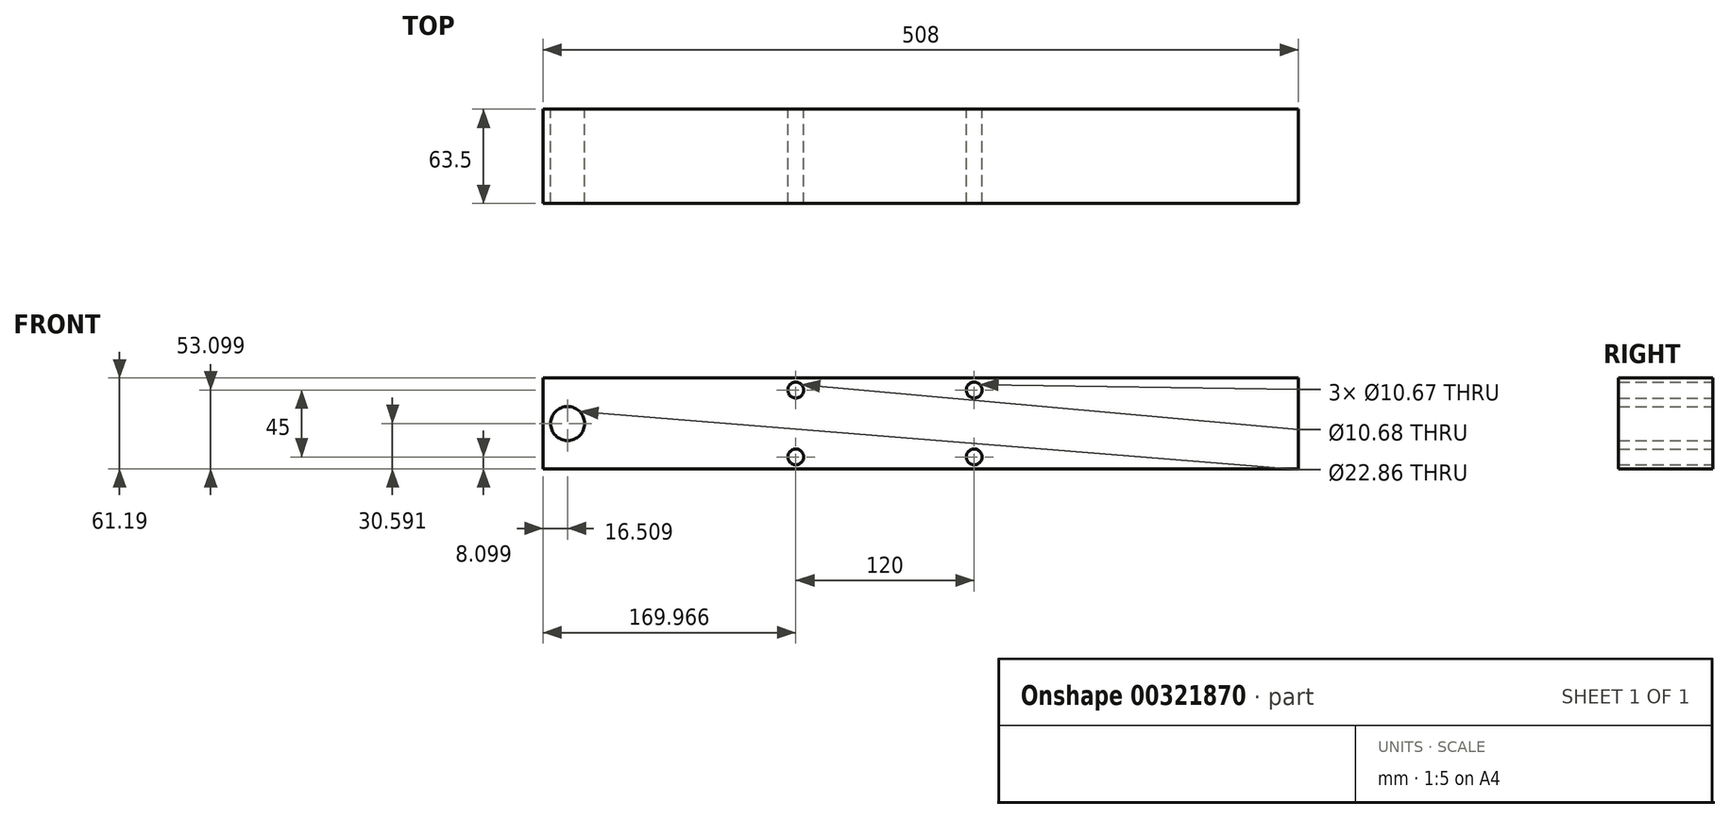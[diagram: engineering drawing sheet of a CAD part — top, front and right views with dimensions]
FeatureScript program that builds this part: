
annotation { "Feature Type Name" : "Feature", "Feature Type Description" : "" }
export const myFeature = defineFeature(function(context is Context, id is Id, definition is map)
    precondition{}
    {
        {
            var Q0;
            Q0=qCreatedBy(makeId("Front.planeOp"),FACE);
            var sketch = newSketch(context, id + "F0", { "sketchPlane" : qUnion([Q0])});
            skLineSegment(sketch, "E0.bottom", {"start": v(-114.58, 33.33) * mm, "end": v(393.42, 33.33) * mm});
            skLineSegment(sketch, "E0.top", {"start": v(-114.58, -27.86) * mm, "end": v(393.42, -27.86) * mm});
            skLineSegment(sketch, "E0.left", {"start": v(-114.58, 33.33) * mm, "end": v(-114.58, -27.86) * mm});
            skLineSegment(sketch, "E0.right", {"start": v(393.42, 33.33) * mm, "end": v(393.42, -27.86) * mm});
            skCircle(sketch, "E1", {"center": v(55.39, 25.24) * mm, "radius": 5.34 * mm});
            skCircle(sketch, "E2", {"center": v(55.39, -19.76) * mm, "radius": 5.33 * mm});
            skCircle(sketch, "E3", {"center": v(175.39, -19.76) * mm, "radius": 5.33 * mm});
            skCircle(sketch, "E4", {"center": v(175.39, 25.24) * mm, "radius": 5.33 * mm});
            skCircle(sketch, "E5", {"center": v(-98.07, 2.73) * mm, "radius": 11.43 * mm});
            skPoint(sketch, "E6", {"position": v(-65.13, 33.33) * mm});
            skSolve(sketch);
        }
        {
            var Q0;
            Q0=makeQuery(id+"F0.imprint","IMPRINT",FACE,{"disambiguationData":[TD([[makeQuery(id+"F0.imprint","IMPRINT",EDGE,{"derivedFrom":sQuery(id+"F0.wireOp",EDGE,"E0.bottom")}),-1.0]])]});
            extrude(context, id + "F1", {"entities" : qUnion([Q0]), "endBound" : BoundingType.SYMMETRIC, "depth" : 63.5 * mm});
        }
    });
